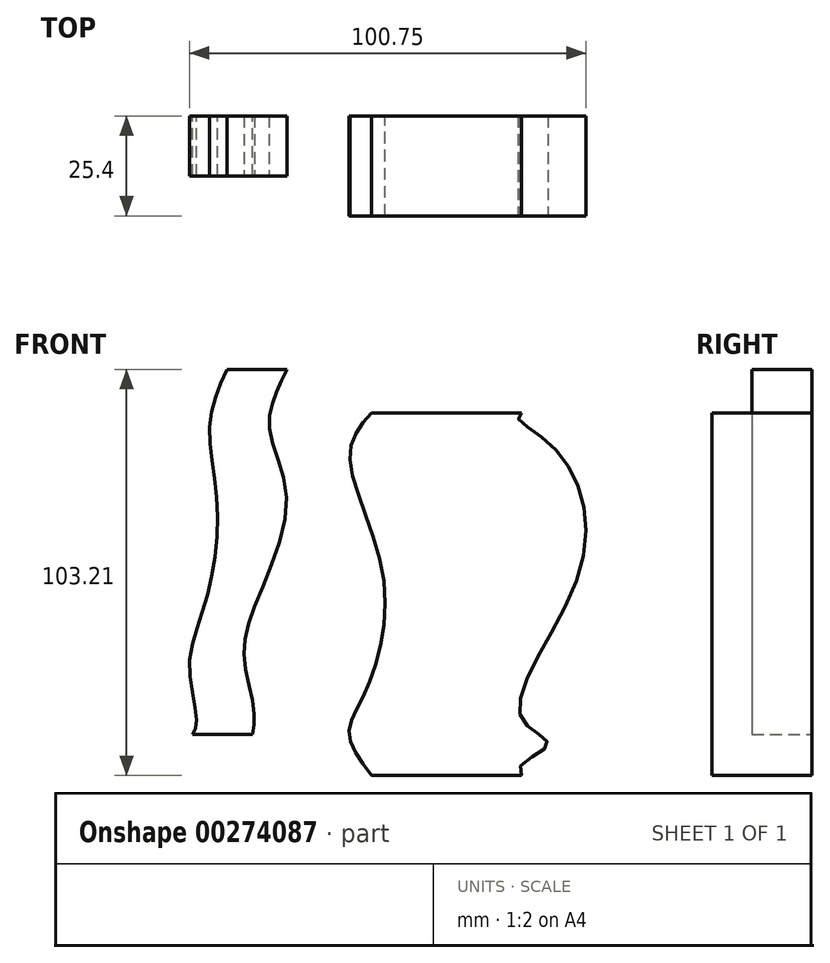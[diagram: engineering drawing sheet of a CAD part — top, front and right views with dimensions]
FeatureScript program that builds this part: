
annotation { "Feature Type Name" : "Feature", "Feature Type Description" : "" }
export const myFeature = defineFeature(function(context is Context, id is Id, definition is map)
    precondition{}
    {
        {
            var Q0;
            Q0=qCreatedBy(makeId("Front.planeOp"),FACE);
            var sketch = newSketch(context, id + "F0", { "sketchPlane" : qUnion([Q0])});
            skLineSegment(sketch, "E0", {"start": v(-26.78, -42.6) * mm, "end": v(11.32, -42.6) * mm});
            skLineSegment(sketch, "E1", {"start": v(-26.78, 49.6) * mm, "end": v(11.32, 49.6) * mm});
            skFitSpline(sketch, "E2", {"points": [v(-26.78, 49.6) * mm, v(-32.25, 38.72) * mm, v(-23.77, 7.94) * mm, v(-28.38, -21.38) * mm, v(-32.43, -31.88) * mm, v(-26.78, -42.6) * mm], "startDerivative": vector(-49.84, -57.12) * mm, "endDerivative": vector(50.48, -68.03) * mm});
            skFitSpline(sketch, "E3", {"points": [v(11.32, 49.6) * mm, v(17.35, 42.78) * mm, v(26.57, 10.9) * mm, v(11.32, -28) * mm, v(17.9, -35.01) * mm, v(11.32, -42.6) * mm], "startDerivative": vector(-62.44, -35.6) * mm, "endDerivative": vector(64.72, -56.26) * mm});
            skSolve(sketch);
        }
        {
            var Q0;
            Q0=makeQuery(id+"F0.imprint","IMPRINT",FACE,{"disambiguationData":[TD([[makeQuery(id+"F0.imprint","IMPRINT",EDGE,{"derivedFrom":sQuery(id+"F0.wireOp",EDGE,"E0")}),1.0]])]});
            extrude(context, id + "F1", {"entities" : qUnion([Q0]), "depth" : 25.4 * mm});
        }
        {
            var Q0;
            Q0=qCreatedBy(makeId("Front.planeOp"),FACE);
            var sketch = newSketch(context, id + "F2", { "sketchPlane" : qUnion([Q0])});
            skLineSegment(sketch, "E4", {"start": v(-63.52, 60.62) * mm, "end": v(-48.28, 60.62) * mm});
            skLineSegment(sketch, "E5", {"start": v(-5.89, 50.34) * mm, "end": v(-5.89, -42.4) * mm});
            skLineSegment(sketch, "E6", {"start": v(-74.98, 60.62) * mm, "end": v(-76.68, -32.07) * mm});
            skLineSegment(sketch, "E7", {"start": v(-72.26, -32.07) * mm, "end": v(-57.02, -32.07) * mm});
            skFitSpline(sketch, "E8", {"points": [v(-63.52, 60.62) * mm, v(-67.84, 46.65) * mm, v(-66, 26.92) * mm, v(-68.76, 2.22) * mm, v(-73, -14.93) * mm, v(-71.15, -28.94) * mm, v(-72.26, -32.07) * mm], "startDerivative": vector(-35.87, -80.93) * mm, "endDerivative": vector(-20.07, -31.48) * mm});
            skFitSpline(sketch, "E9", {"points": [v(-48.28, 60.62) * mm, v(-51.61, 52.92) * mm, v(-52.53, 44.44) * mm, v(-48.28, 26.92) * mm, v(-56.59, 0) * mm, v(-58.98, -13.64) * mm, v(-56.59, -26.17) * mm, v(-57.02, -32.07) * mm], "startDerivative": vector(-31.55, -66.4) * mm, "endDerivative": vector(-10.44, -54.63) * mm});
            skSolve(sketch);
        }
        {
            var Q0;
            Q0=makeQuery(id+"F2.imprint","IMPRINT",FACE,{"disambiguationData":[TD([[makeQuery(id+"F2.imprint","IMPRINT",EDGE,{"derivedFrom":sQuery(id+"F2.wireOp",EDGE,"E4")}),-1.0]])]});
            extrude(context, id + "F3", {"entities" : qUnion([Q0]), "depth" : 15.24 * mm});
        }
    });
